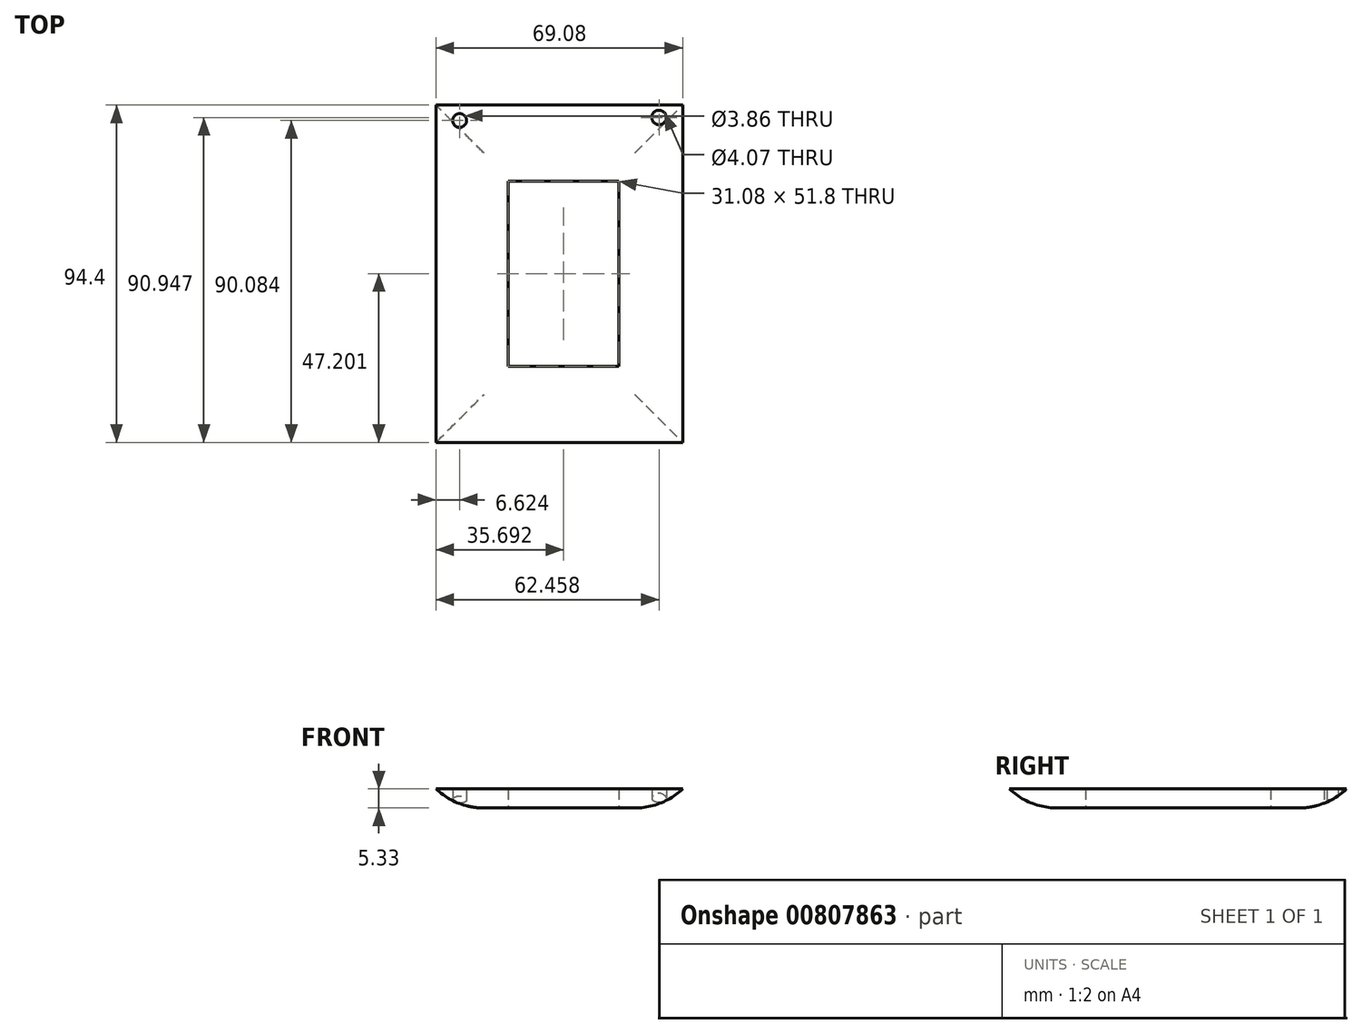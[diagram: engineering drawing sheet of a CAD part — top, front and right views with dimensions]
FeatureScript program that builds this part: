
annotation { "Feature Type Name" : "Feature", "Feature Type Description" : "" }
export const myFeature = defineFeature(function(context is Context, id is Id, definition is map)
    precondition{}
    {
        {
            var Q0;
            Q0=qCreatedBy(makeId("Top.planeOp"),FACE);
            var sketch = newSketch(context, id + "F0", { "sketchPlane" : qUnion([Q0])});
            skLineSegment(sketch, "E0.bottom", {"start": v(-32.67, 46.48) * mm, "end": v(36.4, 46.48) * mm});
            skLineSegment(sketch, "E0.top", {"start": v(-32.67, -47.92) * mm, "end": v(36.4, -47.92) * mm});
            skLineSegment(sketch, "E0.left", {"start": v(-32.67, 46.48) * mm, "end": v(-32.67, -47.92) * mm});
            skLineSegment(sketch, "E0.right", {"start": v(36.4, 46.48) * mm, "end": v(36.4, -47.92) * mm});
            skLineSegment(sketch, "E1.bottom", {"start": v(-12.52, 25.18) * mm, "end": v(18.56, 25.18) * mm});
            skLineSegment(sketch, "E1.top", {"start": v(-12.52, -26.62) * mm, "end": v(18.56, -26.62) * mm});
            skLineSegment(sketch, "E1.left", {"start": v(-12.52, 25.18) * mm, "end": v(-12.52, -26.62) * mm});
            skLineSegment(sketch, "E1.right", {"start": v(18.56, 25.18) * mm, "end": v(18.56, -26.62) * mm});
            skCircle(sketch, "E2", {"center": v(-26.05, 42.16) * mm, "radius": 1.93 * mm});
            skCircle(sketch, "E3", {"center": v(29.79, 43.03) * mm, "radius": 2.04 * mm});
            skSolve(sketch);
        }
        {
            var Q0;
            Q0=makeQuery(id+"F0.imprint","IMPRINT",FACE,{"disambiguationData":[TD([[makeQuery(id+"F0.imprint","IMPRINT",EDGE,{"derivedFrom":sQuery(id+"F0.wireOp",EDGE,"E0.bottom")}),-1.0]])]});
            extrude(context, id + "F1", {"entities" : qUnion([Q0]), "depth" : 5.33 * mm, "offsetDistance" : 25.4 * mm});
        }
        {
            var Q0;
            Q0=makeQuery(id+"F1.opExtrude","CAP_EDGE",EDGE,{"disambiguationData":[OSD([sQuery(id+"F0.wireOp",EDGE,"E0.bottom")])],"isStart":true});
            var Q1;
            Q1=makeQuery(id+"F1.opExtrude","CAP_EDGE",EDGE,{"disambiguationData":[OSD([sQuery(id+"F0.wireOp",EDGE,"E0.right")])],"isStart":true});
            var Q2;
            Q2=makeQuery(id+"F1.opExtrude","CAP_EDGE",EDGE,{"disambiguationData":[OSD([sQuery(id+"F0.wireOp",EDGE,"E0.top")])],"isStart":true});
            var Q3;
            Q3=makeQuery(id+"F1.opExtrude","CAP_EDGE",EDGE,{"disambiguationData":[OSD([sQuery(id+"F0.wireOp",EDGE,"E0.left")])],"isStart":true});
            fillet(context, id + "F2", {"entities" : qUnion([Q0, Q1, Q2, Q3]), "radius" : 19.62 * mm, "tangentPropagation" : true, "allowEdgeOverflow" : false});
        }
    });
